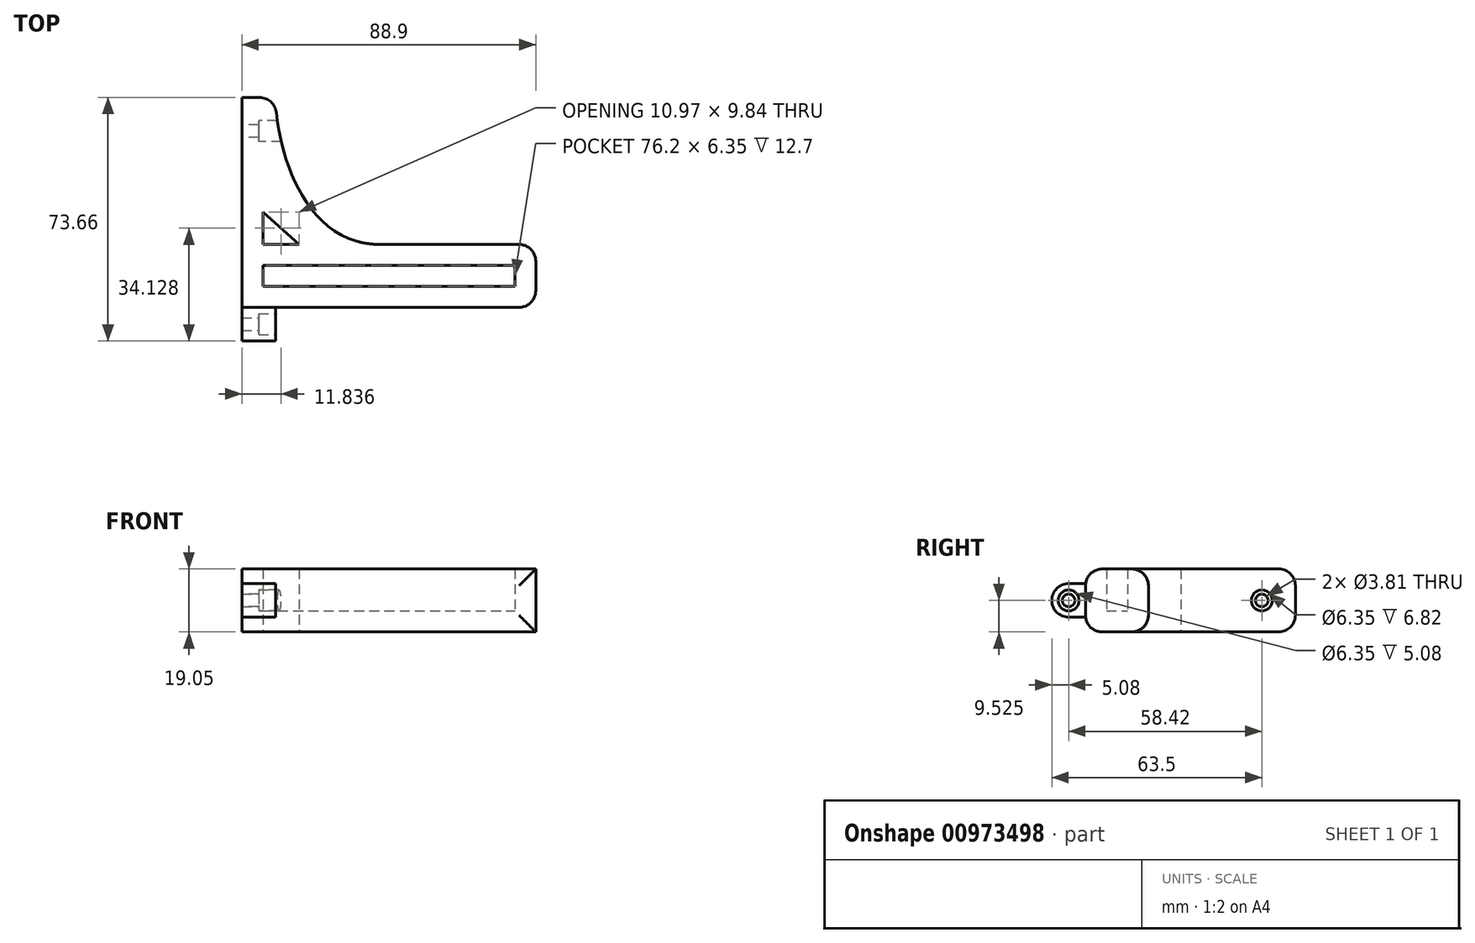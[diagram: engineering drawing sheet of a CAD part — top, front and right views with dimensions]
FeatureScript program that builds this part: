
annotation { "Feature Type Name" : "Feature", "Feature Type Description" : "" }
export const myFeature = defineFeature(function(context is Context, id is Id, definition is map)
    precondition{}
    {
        {
            var Q0;
            Q0=qCreatedBy(makeId("Top.planeOp"),FACE);
            var sketch = newSketch(context, id + "F0", { "sketchPlane" : qUnion([Q0])});
            skLineSegment(sketch, "E0.bottom", {"start": v(0, 0) * mm, "end": v(76.2, 0) * mm});
            skLineSegment(sketch, "E0.top", {"start": v(0, 6.35) * mm, "end": v(76.2, 6.35) * mm});
            skLineSegment(sketch, "E0.left", {"start": v(0, 0) * mm, "end": v(0, 6.35) * mm});
            skLineSegment(sketch, "E0.right", {"start": v(76.2, 0) * mm, "end": v(76.2, 6.35) * mm});
            skLineSegment(sketch, "E1.0", {"start": v(82.55, -6.35) * mm, "end": v(82.55, 12.7) * mm});
            skLineSegment(sketch, "E1.1", {"start": v(-6.35, -6.35) * mm, "end": v(82.55, -6.35) * mm});
            skLineSegment(sketch, "E1.2", {"start": v(-6.35, -6.35) * mm, "end": v(-6.35, 12.7) * mm});
            skLineSegment(sketch, "E1.3", {"start": v(31.6, 12.7) * mm, "end": v(82.55, 12.7) * mm});
            skLineSegment(sketch, "E2", {"start": v(-6.35, 12.7) * mm, "end": v(-6.35, 57.15) * mm});
            skLineSegment(sketch, "E3", {"start": v(-6.35, 57.15) * mm, "end": v(3.8, 57.15) * mm});
            skFitSpline(sketch, "E4", {"points": [v(3.8, 57.15) * mm, v(35.41, 12.7) * mm], "startDerivative": vector(0, -38.1) * mm, "endDerivative": vector(73.32, 0) * mm});
            skPoint(sketch, "E5.orphan", {"position": v(0, 12.7) * mm});
            skLineSegment(sketch, "E6", {"start": v(0, 22.54) * mm, "end": v(10.97, 12.7) * mm});
            skLineSegment(sketch, "E7", {"start": v(0, 22.54) * mm, "end": v(0, 12.7) * mm});
            skLineSegment(sketch, "E8", {"start": v(0, 12.7) * mm, "end": v(10.97, 12.7) * mm});
            skSolve(sketch);
        }
        {
            var Q0;
            Q0=qSketchRegion(id+"F0",true);
            extrude(context, id + "F1", {"entities" : qUnion([Q0]), "depth" : 19.05 * mm, "offsetDistance" : 25.4 * mm});
        }
        {
            var Q0;
            Q0=makeQuery(id+"F0.imprint","IMPRINT",FACE,{"disambiguationData":[TD([[makeQuery(id+"F0.imprint","IMPRINT",EDGE,{"derivedFrom":sQuery(id+"F0.wireOp",EDGE,"E0.bottom")}),1.0]])]});
            extrude(context, id + "F2", {"entities" : qUnion([Q0]), "operationType" : NewBodyOperationType.ADD, "depth" : 6.35 * mm, "offsetDistance" : 25.4 * mm});
        }
        {
            var Q0;
            Q0=makeQuery(id+"F1.opExtrude","SWEPT_FACE",FACE,{"disambiguationData":[OSD([sQuery(id+"F0.wireOp",EDGE,"E1.2"),sQuery(id+"F0.wireOp",EDGE,"E2")])]});
            var sketch = newSketch(context, id + "F3", { "sketchPlane" : qUnion([Q0])});
            skCircle(sketch, "E9", {"center": v(-46.99, 9.53) * mm, "radius": 3.18 * mm});
            skPoint(sketch, "E9.centerSnap0", {"position": v(-57.15, 9.53) * mm});
            skCircle(sketch, "E10", {"center": v(-46.99, 9.53) * mm, "radius": 1.9 * mm});
            skSolve(sketch);
        }
        {
            var Q0;
            Q0=makeQuery(id+"F3.imprint","IMPRINT",FACE,{"disambiguationData":[TD([[makeQuery(id+"F3.imprint","IMPRINT",EDGE,{"derivedFrom":sQuery(id+"F3.wireOp",EDGE,"E9")}),1.0]])]});
            extrude(context, id + "F4", {"entities" : qUnion([Q0]), "operationType" : NewBodyOperationType.REMOVE, "endBound" : BoundingType.UP_TO_NEXT, "oppositeDirection" : true, "depth" : 25.4 * mm, "offsetDistance" : 25.4 * mm, "hasSecondDirection" : true, "secondDirectionOppositeDirection" : true, "secondDirectionDepth" : 5.08 * mm});
        }
        {
            var Q0;
            Q0=makeQuery(id+"F1.opExtrude","SWEPT_FACE",FACE,{"disambiguationData":[OSD([sQuery(id+"F0.wireOp",EDGE,"E1.2"),sQuery(id+"F0.wireOp",EDGE,"E2")])]});
            var sketch = newSketch(context, id + "F5", { "sketchPlane" : qUnion([Q0])});
            skLineSegment(sketch, "E11", {"start": v(6.35, 9.53) * mm, "end": v(17.62, 9.53) * mm, "construction": true});
            skLineSegment(sketch, "E12", {"start": v(6.35, 14.6) * mm, "end": v(11.43, 14.6) * mm});
            skLineSegment(sketch, "E13.MirrorCS", {"start": v(6.35, 4.45) * mm, "end": v(11.43, 4.45) * mm});
            skArc(sketch, "E14", {"start": v(11.43, 4.45) * mm, "mid": v(16.5, 9.53) * mm, "end": v(11.43, 14.6) * mm});
            skSolve(sketch);
        }
        {
            var Q0;
            Q0=qSketchRegion(id+"F5",true);
            var Q1;
            {var subQ0=sQuery(id+"F5.wireOp",EDGE,"E12");Q1=makeQuery(id+"F5.imprint","IMPRINT",FACE,{"disambiguationData":[TD([[makeQuery(id+"F5.imprint","IMPRINT",EDGE,{"derivedFrom":subQ0}),-1.0]])]});}
            extrude(context, id + "F6", {"entities" : qUnion([Q0, Q1]), "operationType" : NewBodyOperationType.ADD, "oppositeDirection" : true, "depth" : 10.16 * mm, "offsetDistance" : 25.4 * mm});
        }
        {
            var Q0;
            Q0=makeQuery(id+"F6.opExtrude","CAP_FACE",FACE,{"disambiguationData":[OSD([sQuery(id+"F0.wireOp",EDGE,"E1.1"),sQuery(id+"F0.wireOp",EDGE,"E1.2"),sQuery(id+"F5.wireOp",EDGE,"E12"),sQuery(id+"F5.wireOp",EDGE,"E13.MirrorCS"),sQuery(id+"F5.wireOp",EDGE,"E14")])],"isStart":false});
            var sketch = newSketch(context, id + "F7", { "sketchPlane" : qUnion([Q0])});
            skCircle(sketch, "E15", {"center": v(-11.43, 9.53) * mm, "radius": 3.18 * mm});
            skCircle(sketch, "E16", {"center": v(-11.43, 9.53) * mm, "radius": 1.9 * mm});
            skSolve(sketch);
        }
        {
            var Q0;
            Q0=qSketchRegion(id+"F7",true);
            extrude(context, id + "F8", {"entities" : qUnion([Q0]), "operationType" : NewBodyOperationType.REMOVE, "oppositeDirection" : true, "depth" : 5.08 * mm, "offsetDistance" : 25.4 * mm});
        }
        {
            var Q0;
            Q0=makeQuery(id+"F7.imprint","IMPRINT",FACE,{"disambiguationData":[TD([[makeQuery(id+"F7.imprint","IMPRINT",EDGE,{"derivedFrom":sQuery(id+"F7.wireOp",EDGE,"E16")}),1.0]])]});
            extrude(context, id + "F9", {"entities" : qUnion([Q0]), "operationType" : NewBodyOperationType.REMOVE, "endBound" : BoundingType.THROUGH_ALL, "oppositeDirection" : true, "depth" : 25.4 * mm, "offsetDistance" : 25.4 * mm});
        }
        {
            var Q0;
            Q0=makeQuery(id+"F3.imprint","IMPRINT",FACE,{"disambiguationData":[TD([[makeQuery(id+"F3.imprint","IMPRINT",EDGE,{"derivedFrom":sQuery(id+"F3.wireOp",EDGE,"E10")}),1.0]])]});
            var Q1;
            Q1=sQuery(id+"F3.wireOp",EDGE,"E10");
            extrude(context, id + "F10", {"entities" : qUnion([Q0]), "operationType" : NewBodyOperationType.REMOVE, "surfaceEntities" : qUnion([Q1]), "endBound" : BoundingType.THROUGH_ALL, "oppositeDirection" : true, "depth" : 25.4 * mm, "offsetDistance" : 25.4 * mm});
        }
        {
            var Q0;
            Q0=makeQuery(id+"F1.opExtrude","CAP_EDGE",EDGE,{"disambiguationData":[OSD([sQuery(id+"F0.wireOp",EDGE,"E1.3")])],"isStart":true});
            var Q1;
            Q1=makeQuery(id+"F1.opExtrude","CAP_EDGE",EDGE,{"disambiguationData":[OSD([sQuery(id+"F0.wireOp",EDGE,"E1.3")])],"isStart":false});
            var Q2;
            Q2=makeQuery(id+"F1.opExtrude","CAP_EDGE",EDGE,{"disambiguationData":[OSD([sQuery(id+"F0.wireOp",EDGE,"E1.1")])],"isStart":false});
            var Q3;
            Q3=makeQuery(id+"F1.opExtrude","CAP_EDGE",EDGE,{"disambiguationData":[OSD([sQuery(id+"F0.wireOp",EDGE,"E1.1")])],"isStart":true});
            var Q4;
            Q4=makeQuery(id+"F1.opExtrude","SWEPT_EDGE",EDGE,{"disambiguationData":[OSD([sQuery(id+"F0.wireOp",EDGE,"E1.0"),sQuery(id+"F0.wireOp",EDGE,"E1.1")])]});
            var Q5;
            Q5=makeQuery(id+"F1.opExtrude","SWEPT_EDGE",EDGE,{"disambiguationData":[OSD([sQuery(id+"F0.wireOp",EDGE,"E1.0"),sQuery(id+"F0.wireOp",EDGE,"E1.3")])]});
            var Q6;
            Q6=makeQuery(id+"F1.opExtrude","SWEPT_EDGE",EDGE,{"disambiguationData":[OSD([sQuery(id+"F0.wireOp",EDGE,"E3"),sQuery(id+"F0.wireOp",EDGE,"E4")])]});
            var Q7;
            Q7=makeQuery(id+"F1.opExtrude","CAP_EDGE",EDGE,{"disambiguationData":[OSD([sQuery(id+"F0.wireOp",EDGE,"E3")])],"isStart":false});
            var Q8;
            Q8=makeQuery(id+"F1.opExtrude","CAP_EDGE",EDGE,{"disambiguationData":[OSD([sQuery(id+"F0.wireOp",EDGE,"E3")])],"isStart":true});
            fillet(context, id + "F11", {"entities" : qUnion([Q0, Q1, Q2, Q3, Q4, Q5, Q6, Q7, Q8]), "radius" : 5.08 * mm, "tangentPropagation" : true, "allowEdgeOverflow" : false});
        }
    });
